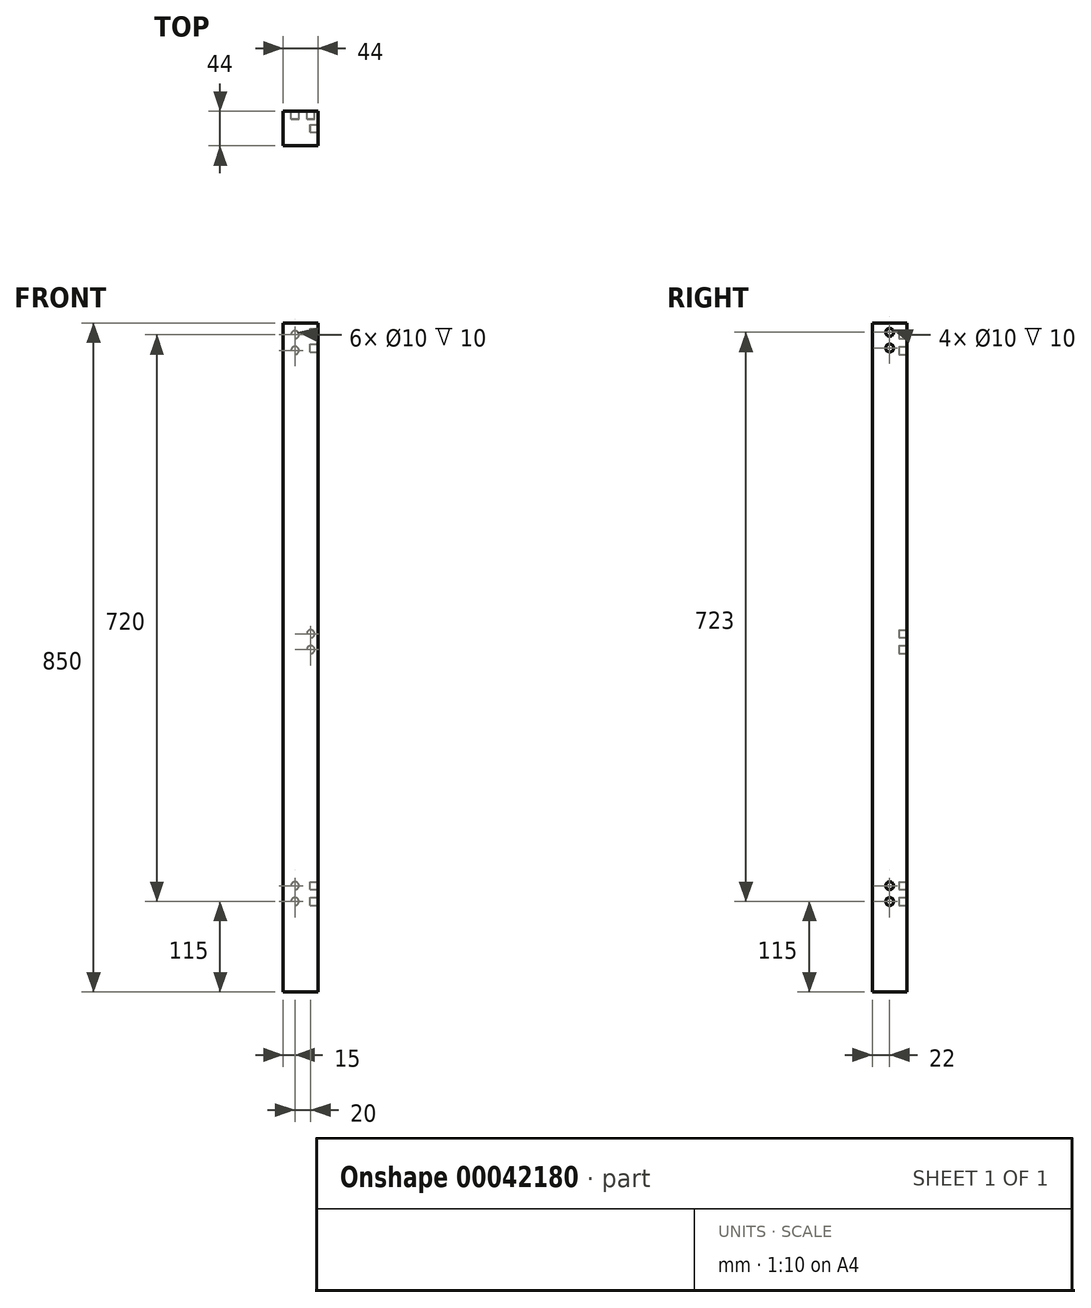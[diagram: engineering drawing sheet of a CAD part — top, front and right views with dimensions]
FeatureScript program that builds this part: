
annotation { "Feature Type Name" : "Feature", "Feature Type Description" : "" }
export const myFeature = defineFeature(function(context is Context, id is Id, definition is map)
    precondition{}
    {
        {
            var Q0;
            Q0=qCreatedBy(makeId("Top.planeOp"),FACE);
            var sketch = newSketch(context, id + "F0", { "sketchPlane" : qUnion([Q0])});
            skLineSegment(sketch, "E0", {"start": v(0, 0) * mm, "end": v(44, 0) * mm});
            skLineSegment(sketch, "E1", {"start": v(44, 0) * mm, "end": v(44, 44) * mm});
            skLineSegment(sketch, "E2", {"start": v(44, 44) * mm, "end": v(0, 44) * mm});
            skLineSegment(sketch, "E3", {"start": v(0, 44) * mm, "end": v(0, 0) * mm});
            skSolve(sketch);
        }
        {
            var Q0;
            Q0=makeQuery(id+"F0.imprint","IMPRINT",FACE,{"disambiguationData":[TD([[makeQuery(id+"F0.imprint","IMPRINT",EDGE,{"derivedFrom":sQuery(id+"F0.wireOp",EDGE,"E0")}),1.0]])]});
            extrude(context, id + "F1", {"entities" : qUnion([Q0]), "depth" : 850 * mm});
        }
        {
            var Q0;
            Q0=makeQuery(id+"F1.opExtrude","SWEPT_FACE",FACE,{"disambiguationData":[OSD([sQuery(id+"F0.wireOp",EDGE,"E2")])]});
            var sketch = newSketch(context, id + "F2", { "sketchPlane" : qUnion([Q0])});
            skCircle(sketch, "E4.1.0.0", {"center": v(-15, 135) * mm, "radius": 5 * mm});
            skLineSegment(sketch, "E4.direction1", {"start": v(-35, 135) * mm, "end": v(-15, 135) * mm, "construction": true});
            skLineSegment(sketch, "E5", {"start": v(-35, 135) * mm, "end": v(-35, 115) * mm, "construction": true});
            skCircle(sketch, "E6.1.0.0", {"center": v(-15, 115) * mm, "radius": 5 * mm});
            skLineSegment(sketch, "E6.direction1", {"start": v(-35, 115) * mm, "end": v(-15, 115) * mm, "construction": true});
            skCircle(sketch, "E7.0.1.0", {"center": v(-35, 435) * mm, "radius": 5 * mm});
            skCircle(sketch, "E7.0.1.2", {"center": v(-30, 1165) * mm, "radius": 5 * mm});
            skLineSegment(sketch, "E7.direction1", {"start": v(-35, 135) * mm, "end": v(-5, 135) * mm, "construction": true});
            skLineSegment(sketch, "E7.direction2", {"start": v(-35, 135) * mm, "end": v(-35, 435) * mm, "construction": true});
            skCircle(sketch, "E8.0.1.0", {"center": v(-15, 835) * mm, "radius": 5 * mm});
            skCircle(sketch, "E8.0.1.1", {"center": v(-15, 815) * mm, "radius": 5 * mm});
            skLineSegment(sketch, "E8.direction2", {"start": v(-15, 135) * mm, "end": v(-15, 835) * mm, "construction": true});
            skCircle(sketch, "E9.0.1.0", {"center": v(-35, 455) * mm, "radius": 5 * mm});
            skLineSegment(sketch, "E9.direction1", {"start": v(-35, 435) * mm, "end": v(-10, 435) * mm, "construction": true});
            skLineSegment(sketch, "E9.direction2", {"start": v(-35, 435) * mm, "end": v(-35, 455) * mm, "construction": true});
            skSolve(sketch);
        }
        {
            var Q0;
            Q0=makeQuery(id+"F2.imprint","IMPRINT",FACE,{"disambiguationData":[TD([[makeQuery(id+"F2.imprint","IMPRINT",EDGE,{"derivedFrom":sQuery(id+"F2.wireOp",EDGE,"8e0a97b6-d979-48df-9837-9e412e9741f4.1.0.0")}),1.0]])]});
            var Q1;
            Q1=makeQuery(id+"F2.imprint","IMPRINT",FACE,{"disambiguationData":[TD([[makeQuery(id+"F2.imprint","IMPRINT",EDGE,{"derivedFrom":sQuery(id+"F2.wireOp",EDGE,"f1c7cc12-a3ff-4c97-8521-861cfaabb000")}),1.0]])]});
            var Q2;
            Q2=makeQuery(id+"F2.imprint","IMPRINT",FACE,{"disambiguationData":[TD([[makeQuery(id+"F2.imprint","IMPRINT",EDGE,{"derivedFrom":sQuery(id+"F2.wireOp",EDGE,"8e0a97b6-d979-48df-9837-9e412e9741f4.0.1.0")}),1.0]])]});
            var Q3;
            Q3=makeQuery(id+"F2.imprint","IMPRINT",FACE,{"disambiguationData":[TD([[makeQuery(id+"F2.imprint","IMPRINT",EDGE,{"derivedFrom":sQuery(id+"F2.wireOp",EDGE,"8e0a97b6-d979-48df-9837-9e412e9741f4.1.1.0")}),1.0]])]});
            var Q4;
            Q4=makeQuery(id+"F2.imprint","IMPRINT",FACE,{"disambiguationData":[TD([[makeQuery(id+"F2.imprint","IMPRINT",EDGE,{"derivedFrom":sQuery(id+"F2.wireOp",EDGE,"ccbc5ad0-b777-4d08-b189-fa7c7758df6a")}),1.0]])]});
            var Q5;
            Q5=makeQuery(id+"F2.imprint","IMPRINT",FACE,{"disambiguationData":[TD([[makeQuery(id+"F2.imprint","IMPRINT",EDGE,{"derivedFrom":sQuery(id+"F2.wireOp",EDGE,"E6.1.0.0")}),1.0]])]});
            var Q6;
            Q6=makeQuery(id+"F2.imprint","IMPRINT",FACE,{"disambiguationData":[TD([[makeQuery(id+"F2.imprint","IMPRINT",EDGE,{"derivedFrom":sQuery(id+"F2.wireOp",EDGE,"E4.1.0.0")}),1.0]])]});
            var Q7;
            Q7=makeQuery(id+"F2.imprint","IMPRINT",FACE,{"disambiguationData":[TD([[makeQuery(id+"F2.imprint","IMPRINT",EDGE,{"derivedFrom":sQuery(id+"F2.wireOp",EDGE,"5b8f005e-ab5e-45a1-8896-f62780331266")}),1.0]])]});
            var Q8;
            Q8=makeQuery(id+"F2.imprint","IMPRINT",FACE,{"disambiguationData":[TD([[makeQuery(id+"F2.imprint","IMPRINT",EDGE,{"derivedFrom":sQuery(id+"F2.wireOp",EDGE,"8b778c67-40aa-4754-9ee9-b491fac5ca7c.0.1.0")}),1.0]])]});
            var Q9;
            Q9=makeQuery(id+"F2.imprint","IMPRINT",FACE,{"disambiguationData":[TD([[makeQuery(id+"F2.imprint","IMPRINT",EDGE,{"derivedFrom":sQuery(id+"F2.wireOp",EDGE,"8b778c67-40aa-4754-9ee9-b491fac5ca7c.0.1.1")}),1.0]])]});
            var Q10;
            Q10=makeQuery(id+"F2.imprint","IMPRINT",FACE,{"disambiguationData":[TD([[makeQuery(id+"F2.imprint","IMPRINT",EDGE,{"derivedFrom":sQuery(id+"F2.wireOp",EDGE,"E7.0.1.0")}),1.0]])]});
            var Q11;
            Q11=makeQuery(id+"F2.imprint","IMPRINT",FACE,{"disambiguationData":[TD([[makeQuery(id+"F2.imprint","IMPRINT",EDGE,{"derivedFrom":sQuery(id+"F2.wireOp",EDGE,"E7.0.1.1")}),1.0]])]});
            var Q12;
            Q12=makeQuery(id+"F2.imprint","IMPRINT",FACE,{"disambiguationData":[TD([[makeQuery(id+"F2.imprint","IMPRINT",EDGE,{"derivedFrom":sQuery(id+"F2.wireOp",EDGE,"E8.0.1.0")}),1.0]])]});
            var Q13;
            Q13=makeQuery(id+"F2.imprint","IMPRINT",FACE,{"disambiguationData":[TD([[makeQuery(id+"F2.imprint","IMPRINT",EDGE,{"derivedFrom":sQuery(id+"F2.wireOp",EDGE,"E8.0.1.1")}),1.0]])]});
            var Q14;
            Q14=makeQuery(id+"F2.imprint","IMPRINT",FACE,{"disambiguationData":[TD([[makeQuery(id+"F2.imprint","IMPRINT",EDGE,{"derivedFrom":sQuery(id+"F2.wireOp",EDGE,"E9.0.1.0")}),1.0]])]});
            extrude(context, id + "F3", {"entities" : qUnion([Q0, Q1, Q2, Q3, Q4, Q5, Q6, Q7, Q8, Q9, Q10, Q11, Q12, Q13, Q14]), "operationType" : NewBodyOperationType.REMOVE, "oppositeDirection" : true, "depth" : 10 * mm});
        }
        {
            var Q0;
            Q0=makeQuery(id+"F1.opExtrude","SWEPT_FACE",FACE,{"disambiguationData":[OSD([sQuery(id+"F0.wireOp",EDGE,"E1")])]});
            var sketch = newSketch(context, id + "F4", { "sketchPlane" : qUnion([Q0])});
            skCircle(sketch, "E10", {"center": v(22, 135) * mm, "radius": 5 * mm});
            skCircle(sketch, "E11.0.1.0", {"center": v(22, 115) * mm, "radius": 5 * mm});
            skLineSegment(sketch, "E11.direction1", {"start": v(22, 135) * mm, "end": v(35, 135) * mm, "construction": true});
            skLineSegment(sketch, "E11.direction2", {"start": v(22, 135) * mm, "end": v(22, 115) * mm, "construction": true});
            skCircle(sketch, "E12.0.1.0", {"center": v(22, 838) * mm, "radius": 5 * mm});
            skCircle(sketch, "E12.0.1.1", {"center": v(22, 818) * mm, "radius": 5 * mm});
            skLineSegment(sketch, "E12.direction2", {"start": v(22, 135) * mm, "end": v(22, 838) * mm, "construction": true});
            skSolve(sketch);
        }
        {
            var Q0;
            Q0=makeQuery(id+"F4.imprint","IMPRINT",FACE,{"disambiguationData":[TD([[makeQuery(id+"F4.imprint","IMPRINT",EDGE,{"derivedFrom":sQuery(id+"F4.wireOp",EDGE,"E10")}),1.0]])]});
            var Q1;
            Q1=makeQuery(id+"F4.imprint","IMPRINT",FACE,{"disambiguationData":[TD([[makeQuery(id+"F4.imprint","IMPRINT",EDGE,{"derivedFrom":sQuery(id+"F4.wireOp",EDGE,"E11.0.1.0")}),1.0]])]});
            var Q2;
            Q2=makeQuery(id+"F4.imprint","IMPRINT",FACE,{"disambiguationData":[TD([[makeQuery(id+"F4.imprint","IMPRINT",EDGE,{"derivedFrom":sQuery(id+"F4.wireOp",EDGE,"E12.0.1.0")}),1.0]])]});
            var Q3;
            Q3=makeQuery(id+"F4.imprint","IMPRINT",FACE,{"disambiguationData":[TD([[makeQuery(id+"F4.imprint","IMPRINT",EDGE,{"derivedFrom":sQuery(id+"F4.wireOp",EDGE,"E12.0.1.1")}),1.0]])]});
            extrude(context, id + "F5", {"entities" : qUnion([Q0, Q1, Q2, Q3]), "operationType" : NewBodyOperationType.REMOVE, "oppositeDirection" : true, "depth" : 10 * mm});
        }
    });
